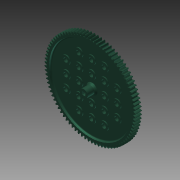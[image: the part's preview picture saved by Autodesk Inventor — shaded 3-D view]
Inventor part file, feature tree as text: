
AUTODESK INVENTOR PART (.ipt)
format: ipt  version: 2013 (Build 170138000, 138)  size: 1,238,528 bytes
history: native  units: mm (DEFAULTED — no unit token found)
features: imported_body x1, sketch x1, other x1, extrude x1
ambient origin geometry x8: Origin, YZ Plane, XZ Plane, XY Plane, X Axis, Y Axis, Z Axis, Center Point
bodies: Solid1 (feature_tree)
feature tree (4):
  imported_body  "Base1"
  sketch  "Sketch1"  dims[d1=8.001mm d5=25.4mm d6=0.0mm d7=0.0mm d8=0.0mm]
  other  "Srf1"
  extrude  "ExtrusionSrf1"  Depth=25.4mm TaperAngle=0.0deg
